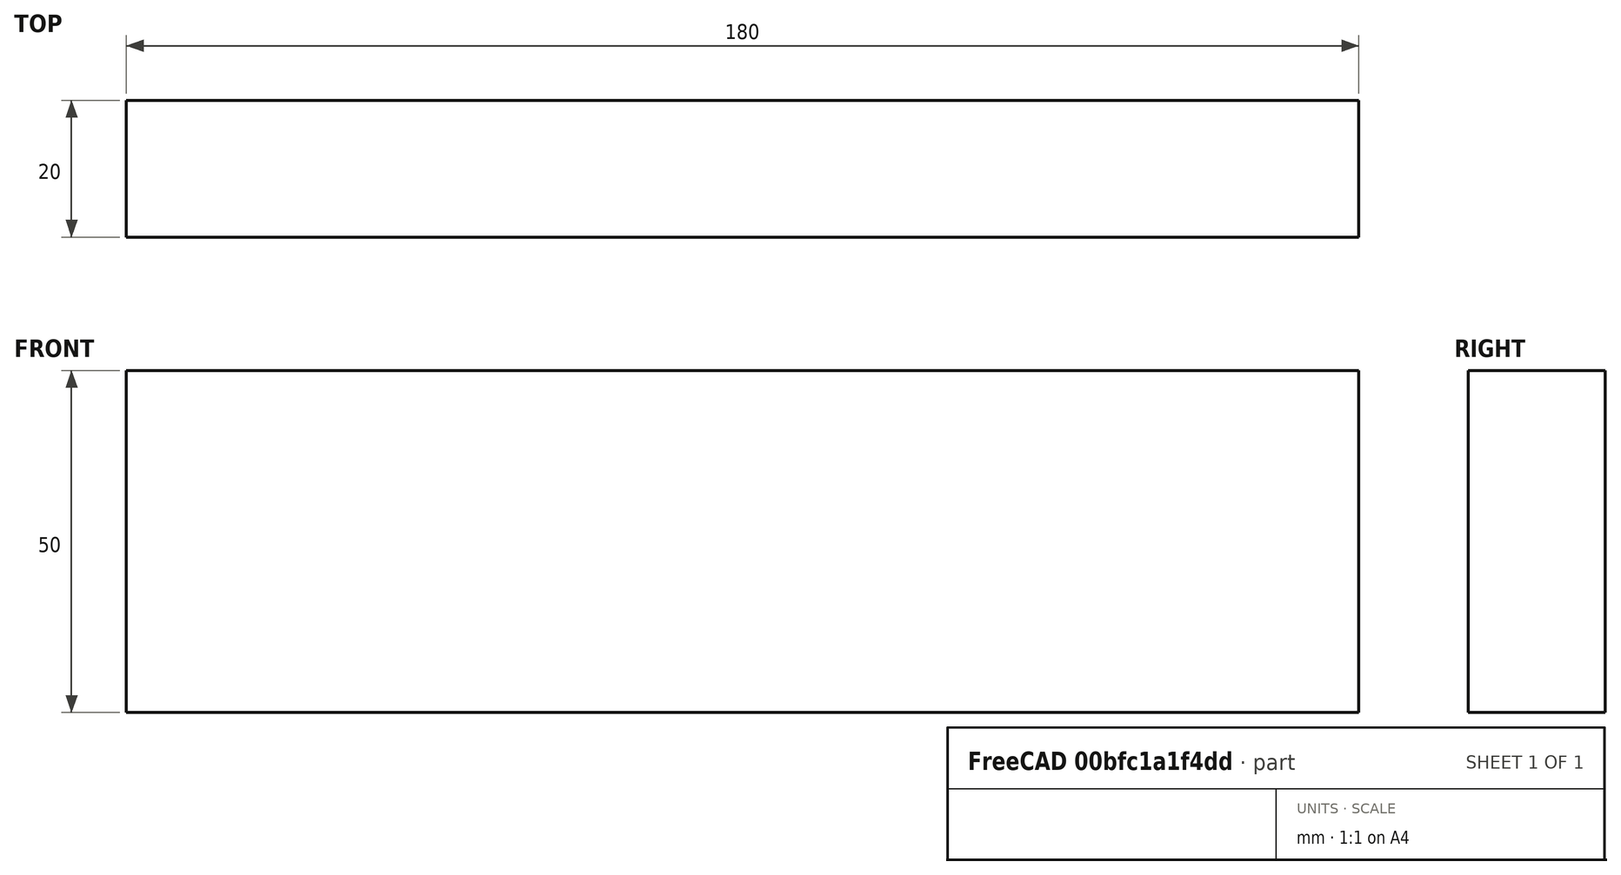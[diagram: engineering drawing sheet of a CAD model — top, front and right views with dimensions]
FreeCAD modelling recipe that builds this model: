
FCSTD DOCUMENT  (FreeCAD 0.15R4671 (Git))
Label: Flat Bar 180x20 EN10058 S235JR
License: All rights reserved
LicenseURL: http://en.wikipedia.org/wiki/All_rights_reserved
objects: Sketcher::SketchObject×1, Part::Extrusion×1
note: 2 computed .brp shape members not serialized (recipe doc carries the construction recipe); baked Part::Feature solids carry a one-line shape summary decoded from their .brp

FEATURE [Sketcher::SketchObject] Sketch
  sketch-geometry (4):
    g0: LineSegment StartX=-90 StartY=-10 StartZ=0 EndX=90 EndY=-10 EndZ=0
    g1: LineSegment StartX=90 StartY=-10 StartZ=0 EndX=90 EndY=10 EndZ=0
    g2: LineSegment StartX=90 StartY=10 StartZ=0 EndX=-90 EndY=10 EndZ=0
    g3: LineSegment StartX=-90 StartY=10 StartZ=0 EndX=-90 EndY=-10 EndZ=0
  constraints (12):
    c: Coincident(g0,g1)
    c: Coincident(g1,g2)
    c: Coincident(g2,g3)
    c: Coincident(g3,g0)
    c: Horizontal(g0)
    c: Horizontal(g2)
    c: Vertical(g1)
    c: Vertical(g3)
    c: Symmetric(g1,g2,g-2)
    c: Symmetric(g0,g1,g-1)
    c: DistanceY(g1) = 20
    c: DistanceX(g0) = 180
FEATURE [Part::Extrusion] Extrude  label="Flat Bar 180x20 EN10058 S235JR"
  Base = -> Sketch
  Dir = (0,0,50)
  Solid = true
